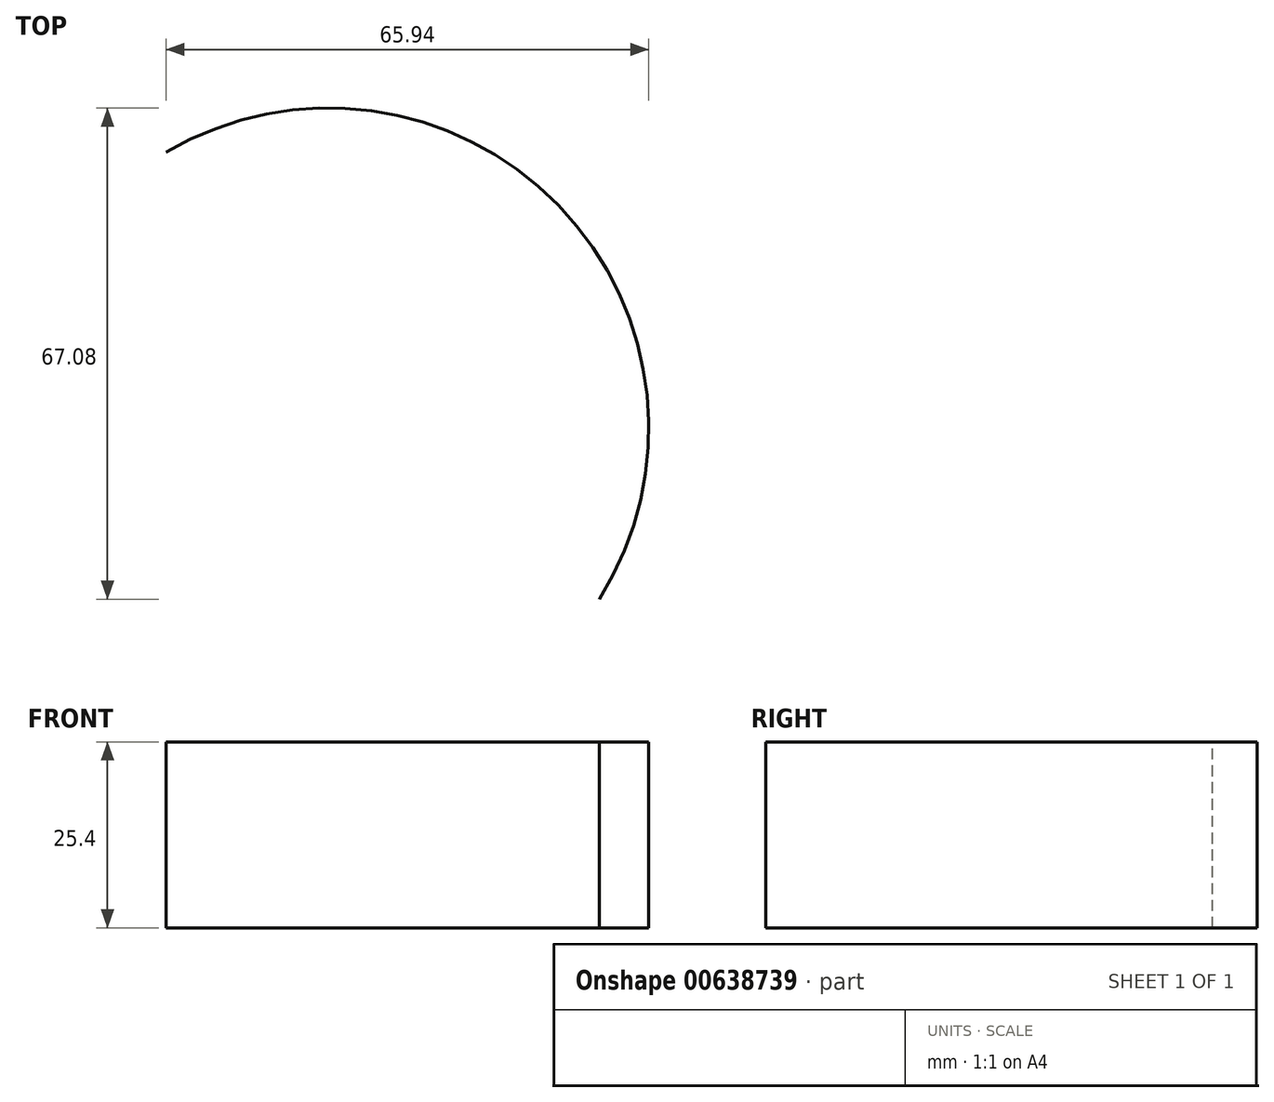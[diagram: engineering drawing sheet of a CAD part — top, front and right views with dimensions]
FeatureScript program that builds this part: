
annotation { "Feature Type Name" : "Feature", "Feature Type Description" : "" }
export const myFeature = defineFeature(function(context is Context, id is Id, definition is map)
    precondition{}
    {
        {
            var Q0;
            Q0=qCreatedBy(makeId("Top.planeOp"),FACE);
            var sketch = newSketch(context, id + "F0", { "sketchPlane" : qUnion([Q0])});
            skArc(sketch, "E0", {"start": v(0, 0) * mm, "mid": v(-5.6, 53.8) * mm, "end": v(-59.19, 61.04) * mm});
            skSolve(sketch);
        }
        {
            var Q0;
            Q0=sQuery(id+"F0.wireOp",EDGE,"E0");
            extrude(context, id + "F1", {"bodyType" : ToolBodyType.SURFACE, "surfaceEntities" : qUnion([Q0]), "depth" : 25.4 * mm, "offsetDistance" : 25.4 * mm});
        }
    });
